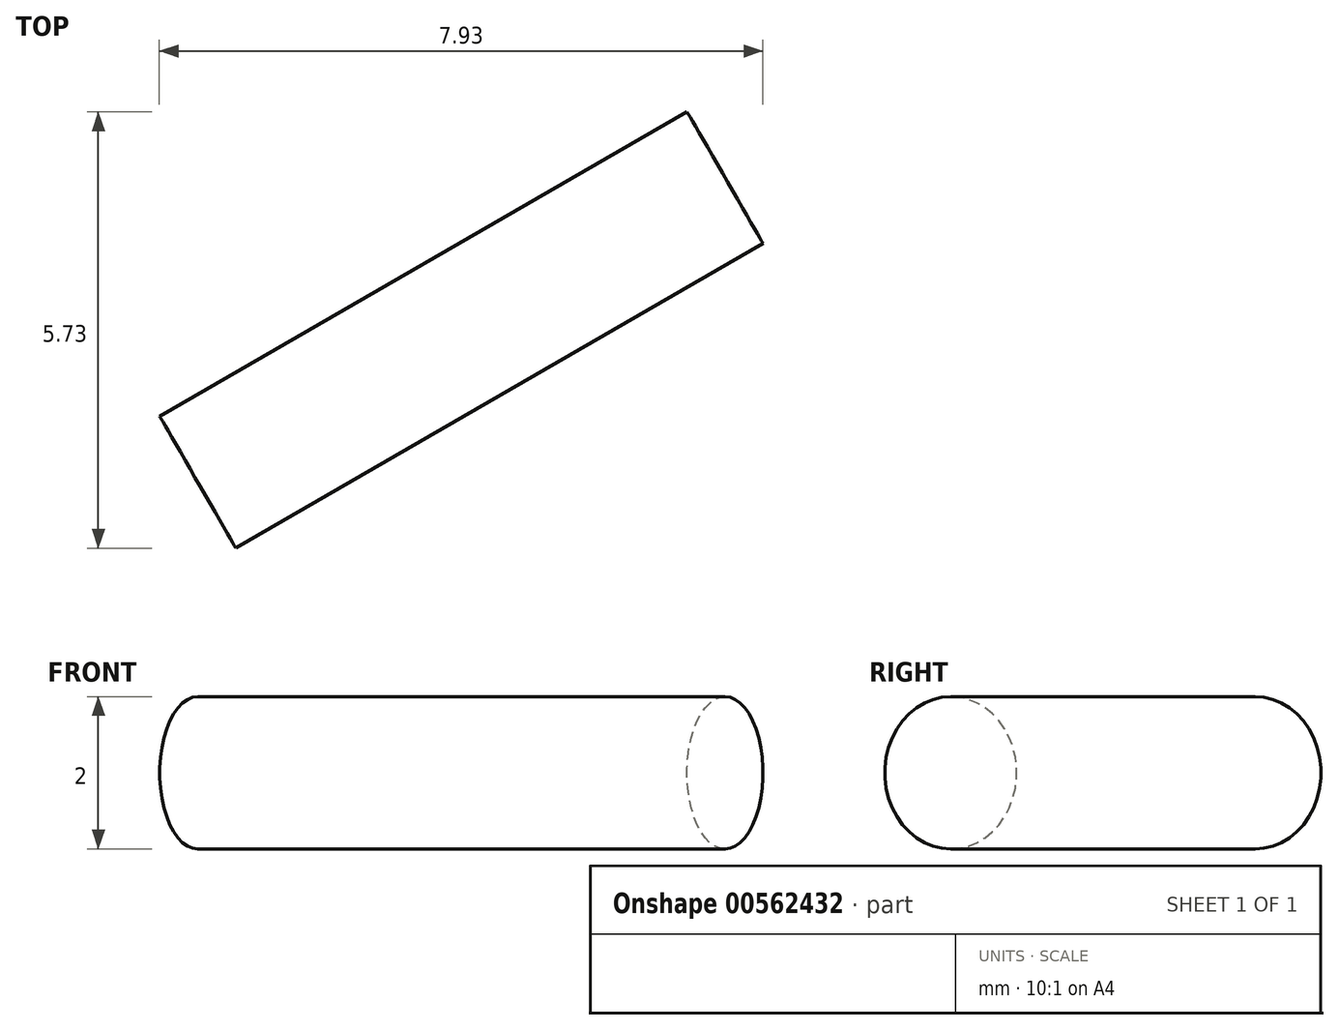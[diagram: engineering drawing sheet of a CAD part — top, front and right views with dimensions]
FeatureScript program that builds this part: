
annotation { "Feature Type Name" : "Feature", "Feature Type Description" : "" }
export const myFeature = defineFeature(function(context is Context, id is Id, definition is map)
    precondition{}
    {
        {
            var Q0;
            Q0=qCreatedBy(makeId("Right.planeOp"),FACE);
            var sketch = newSketch(context, id + "F0", { "sketchPlane" : qUnion([Q0])});
            skCircle(sketch, "E0", {"center": v(0, 0) * mm, "radius": 1 * mm});
            skSolve(sketch);
        }
        {
            var Q0;
            Q0 = qSketchRegion(id + "F0", true);
            extrude(context, id + "F1", {"entities" : qUnion([Q0]), "depth" : 8 * mm, "offsetDistance" : 25 * mm});
        }
        {
            var Q0;
            Q0=makeQuery(id+"F1.opExtrude","SWEPT_BODY",BODY,{"disambiguationData":[OSD([sQuery(id+"F0.wireOp",EDGE,"E0")])]});
            var Q1;
            Q1=makeQuery(id+"F1.opExtrude","CAP_EDGE",EDGE,{"disambiguationData":[OSD([sQuery(id+"F0.wireOp",EDGE,"E0")])],"isStart":true});
            transform(context, id + "F2", {"entities" : qUnion([Q0]), "transformType" : TransformType.ROTATION, "transformAxis" : qUnion([Q1]), "angle" : 45 * degree, "makeCopy" : true});
        }
        {
            var Q0;
            Q0=qCreatedBy(makeId("Right.planeOp"),FACE);
            var sketch = newSketch(context, id + "F3", { "sketchPlane" : qUnion([Q0])});
            skLineSegment(sketch, "E1.bottom", {"start": v(4.5, -1.48) * mm, "end": v(-8.5, -1.48) * mm});
            skLineSegment(sketch, "E1.top", {"start": v(4.5, 1.52) * mm, "end": v(-8.5, 1.52) * mm});
            skLineSegment(sketch, "E1.left", {"start": v(4.5, -1.48) * mm, "end": v(4.5, 1.52) * mm});
            skLineSegment(sketch, "E1.right", {"start": v(-8.5, -1.48) * mm, "end": v(-8.5, 1.52) * mm});
            skSolve(sketch);
        }
        {
            var Q0;
            Q0 = qSketchRegion(id + "F3", true);
            extrude(context, id + "F4", {"entities" : qUnion([Q0]), "endBound" : BoundingType.SYMMETRIC, "depth" : 2.5 * mm, "offsetDistance" : 25 * mm});
        }
        {
            var Q0;
            Q0=makeQuery(id+"F1.opExtrude","SWEPT_BODY",BODY,{"disambiguationData":[OSD([sQuery(id+"F0.wireOp",EDGE,"E0")])]});
            var Q1;
            Q1=makeQuery(id+"F4.opExtrude","CAP_EDGE",EDGE,{"disambiguationData":[OSD([sQuery(id+"F3.wireOp",EDGE,"E1.left")])],"isStart":true});
            transform(context, id + "F5", {"entities" : qUnion([Q0]), "transformType" : TransformType.ROTATION, "transformAxis" : qUnion([Q1]), "angle" : 30 * degree, "makeCopy" : false});
        }
        {
            var Q0;
            Q0=makeQuery(id+"F4.opExtrude","CAP_EDGE",EDGE,{"disambiguationData":[OSD([sQuery(id+"F3.wireOp",EDGE,"E1.bottom")])],"isStart":true});
            var Q1;
            Q1=makeQuery(id+"F4.opExtrude","CAP_EDGE",EDGE,{"disambiguationData":[OSD([sQuery(id+"F3.wireOp",EDGE,"E1.bottom")])],"isStart":false});
            var Q2;
            Q2=makeQuery(id+"F4.opExtrude","CAP_EDGE",EDGE,{"disambiguationData":[OSD([sQuery(id+"F3.wireOp",EDGE,"E1.top")])],"isStart":true});
            var Q3;
            Q3=makeQuery(id+"F4.opExtrude","CAP_EDGE",EDGE,{"disambiguationData":[OSD([sQuery(id+"F3.wireOp",EDGE,"E1.top")])],"isStart":false});
            chamfer(context, id + "F6", {"entities" : qUnion([Q0, Q1, Q2, Q3]), "width" : .5 * mm, "tangentPropagation" : true});
        }
        {
            var Q0;
            Q0=makeQuery(id+"F4.opExtrude","CAP_EDGE",EDGE,{"disambiguationData":[OSD([sQuery(id+"F3.wireOp",EDGE,"E1.right")])],"isStart":true});
            var Q1;
            Q1=makeQuery(id+"F4.opExtrude","CAP_EDGE",EDGE,{"disambiguationData":[OSD([sQuery(id+"F3.wireOp",EDGE,"E1.right")])],"isStart":false});
            var Q2;
            Q2=makeQuery(id+"F6.opChamfer","BLEND_EDGE",EDGE,{"blendedFrom":[makeQuery(id+"F4.opExtrude","CAP_EDGE",EDGE,{"disambiguationData":[OSD([sQuery(id+"F3.wireOp",EDGE,"E1.top")])],"isStart":true}),makeQuery(id+"F4.opExtrude","SWEPT_FACE",FACE,{"disambiguationData":[OSD([sQuery(id+"F3.wireOp",EDGE,"E1.right")])]})],"blendedInto":[makeQuery(id+"F4.opExtrude","SWEPT_FACE",FACE,{"disambiguationData":[OSD([sQuery(id+"F3.wireOp",EDGE,"E1.right")])]})]});
            var Q3;
            Q3=makeQuery(id+"F6.opChamfer","BLEND_EDGE",EDGE,{"blendedFrom":[makeQuery(id+"F4.opExtrude","CAP_EDGE",EDGE,{"disambiguationData":[OSD([sQuery(id+"F3.wireOp",EDGE,"E1.bottom")])],"isStart":true}),makeQuery(id+"F4.opExtrude","SWEPT_FACE",FACE,{"disambiguationData":[OSD([sQuery(id+"F3.wireOp",EDGE,"E1.right")])]})],"blendedInto":[makeQuery(id+"F4.opExtrude","SWEPT_FACE",FACE,{"disambiguationData":[OSD([sQuery(id+"F3.wireOp",EDGE,"E1.right")])]})]});
            var Q4;
            Q4=makeQuery(id+"F6.opChamfer","BLEND_EDGE",EDGE,{"blendedFrom":[makeQuery(id+"F4.opExtrude","CAP_EDGE",EDGE,{"disambiguationData":[OSD([sQuery(id+"F3.wireOp",EDGE,"E1.top")])],"isStart":false}),makeQuery(id+"F4.opExtrude","SWEPT_FACE",FACE,{"disambiguationData":[OSD([sQuery(id+"F3.wireOp",EDGE,"E1.right")])]})],"blendedInto":[makeQuery(id+"F4.opExtrude","SWEPT_FACE",FACE,{"disambiguationData":[OSD([sQuery(id+"F3.wireOp",EDGE,"E1.right")])]})]});
            var Q5;
            Q5=makeQuery(id+"F6.opChamfer","BLEND_EDGE",EDGE,{"blendedFrom":[makeQuery(id+"F4.opExtrude","CAP_EDGE",EDGE,{"disambiguationData":[OSD([sQuery(id+"F3.wireOp",EDGE,"E1.bottom")])],"isStart":false}),makeQuery(id+"F4.opExtrude","SWEPT_FACE",FACE,{"disambiguationData":[OSD([sQuery(id+"F3.wireOp",EDGE,"E1.right")])]})],"blendedInto":[makeQuery(id+"F4.opExtrude","SWEPT_FACE",FACE,{"disambiguationData":[OSD([sQuery(id+"F3.wireOp",EDGE,"E1.right")])]})]});
            chamfer(context, id + "F7", {"entities" : qUnion([Q0, Q1, Q2, Q3, Q4, Q5]), "chamferType" : ChamferType.TWO_OFFSETS, "width1" : .5 * mm, "oppositeDirection" : false, "width2" : .5 * mm, "tangentPropagation" : true});
        }
        {
            var Q0;
            Q0=makeQuery(id+"F6.opChamfer","BLEND_EDGE",EDGE,{"blendedFrom":[makeQuery(id+"F4.opExtrude","CAP_EDGE",EDGE,{"disambiguationData":[OSD([sQuery(id+"F3.wireOp",EDGE,"E1.top")])],"isStart":true}),makeQuery(id+"F4.opExtrude","SWEPT_FACE",FACE,{"disambiguationData":[OSD([sQuery(id+"F3.wireOp",EDGE,"E1.left")])]})],"blendedInto":[makeQuery(id+"F4.opExtrude","SWEPT_FACE",FACE,{"disambiguationData":[OSD([sQuery(id+"F3.wireOp",EDGE,"E1.left")])]})]});
            var Q1;
            Q1=makeQuery(id+"F6.opChamfer","BLEND_EDGE",EDGE,{"blendedFrom":[makeQuery(id+"F4.opExtrude","CAP_EDGE",EDGE,{"disambiguationData":[OSD([sQuery(id+"F3.wireOp",EDGE,"E1.top")])],"isStart":false}),makeQuery(id+"F4.opExtrude","SWEPT_FACE",FACE,{"disambiguationData":[OSD([sQuery(id+"F3.wireOp",EDGE,"E1.left")])]})],"blendedInto":[makeQuery(id+"F4.opExtrude","SWEPT_FACE",FACE,{"disambiguationData":[OSD([sQuery(id+"F3.wireOp",EDGE,"E1.left")])]})]});
            var Q2;
            Q2=makeQuery(id+"F6.opChamfer","BLEND_EDGE",EDGE,{"blendedFrom":[makeQuery(id+"F4.opExtrude","CAP_EDGE",EDGE,{"disambiguationData":[OSD([sQuery(id+"F3.wireOp",EDGE,"E1.bottom")])],"isStart":true}),makeQuery(id+"F4.opExtrude","SWEPT_FACE",FACE,{"disambiguationData":[OSD([sQuery(id+"F3.wireOp",EDGE,"E1.left")])]})],"blendedInto":[makeQuery(id+"F4.opExtrude","SWEPT_FACE",FACE,{"disambiguationData":[OSD([sQuery(id+"F3.wireOp",EDGE,"E1.left")])]})]});
            var Q3;
            Q3=makeQuery(id+"F6.opChamfer","BLEND_EDGE",EDGE,{"blendedFrom":[makeQuery(id+"F4.opExtrude","CAP_EDGE",EDGE,{"disambiguationData":[OSD([sQuery(id+"F3.wireOp",EDGE,"E1.bottom")])],"isStart":false}),makeQuery(id+"F4.opExtrude","SWEPT_FACE",FACE,{"disambiguationData":[OSD([sQuery(id+"F3.wireOp",EDGE,"E1.left")])]})],"blendedInto":[makeQuery(id+"F4.opExtrude","SWEPT_FACE",FACE,{"disambiguationData":[OSD([sQuery(id+"F3.wireOp",EDGE,"E1.left")])]})]});
            var Q4;
            {var subQ0=sQuery(id+"F3.wireOp",EDGE,"E1.right");Q4=makeQuery(id+"F7.opChamfer","BLEND_EDGE",EDGE,{"blendedFrom":[makeQuery(id+"F4.opExtrude","CAP_EDGE",EDGE,{"disambiguationData":[OSD([subQ0])],"isStart":true}),makeQuery(id+"F4.opExtrude","CAP_FACE",FACE,{"disambiguationData":[OSD([sQuery(id+"F3.wireOp",EDGE,"E1.bottom"),sQuery(id+"F3.wireOp",EDGE,"E1.top"),sQuery(id+"F3.wireOp",EDGE,"E1.left"),subQ0])],"isStart":true})],"blendedInto":[makeQuery(id+"F4.opExtrude","CAP_FACE",FACE,{"disambiguationData":[OSD([sQuery(id+"F3.wireOp",EDGE,"E1.bottom"),sQuery(id+"F3.wireOp",EDGE,"E1.top"),sQuery(id+"F3.wireOp",EDGE,"E1.left"),subQ0])],"isStart":true})]});}
            var Q5;
            {var subQ0=sQuery(id+"F3.wireOp",EDGE,"E1.right");Q5=makeQuery(id+"F7.opChamfer","BLEND_EDGE",EDGE,{"blendedFrom":[makeQuery(id+"F4.opExtrude","CAP_EDGE",EDGE,{"disambiguationData":[OSD([subQ0])],"isStart":false}),makeQuery(id+"F4.opExtrude","CAP_FACE",FACE,{"disambiguationData":[OSD([sQuery(id+"F3.wireOp",EDGE,"E1.bottom"),sQuery(id+"F3.wireOp",EDGE,"E1.top"),sQuery(id+"F3.wireOp",EDGE,"E1.left"),subQ0])],"isStart":false})],"blendedInto":[makeQuery(id+"F4.opExtrude","CAP_FACE",FACE,{"disambiguationData":[OSD([sQuery(id+"F3.wireOp",EDGE,"E1.bottom"),sQuery(id+"F3.wireOp",EDGE,"E1.top"),sQuery(id+"F3.wireOp",EDGE,"E1.left"),subQ0])],"isStart":false})]});}
            fillet(context, id + "F8", {"entities" : qUnion([Q0, Q1, Q2, Q3, Q4, Q5]), "radius" : 2.5 * mm, "tangentPropagation" : true, "allowEdgeOverflow" : false});
        }
        {
            var Q0;
            Q0=makeQuery(id+"F1.opExtrude","SWEPT_BODY",BODY,{"disambiguationData":[OSD([sQuery(id+"F0.wireOp",EDGE,"E0")])]});
            var Q1;
            Q1=qCreatedBy(makeId("Right.planeOp"),FACE);
            transform(context, id + "F9", {"entities" : qUnion([Q0]), "transformType" : TransformType.TRANSLATION_DISTANCE, "transformDirection" : qUnion([Q1]), "distance" : 1.75 * mm, "oppositeDirection" : true, "makeCopy" : false});
        }
        {
            var Q0;
            Q0=qCreatedBy(makeId("Front.planeOp"),FACE);
            var sketch = newSketch(context, id + "F10", { "sketchPlane" : qUnion([Q0])});
            skCircle(sketch, "E2", {"center": v(0, 0) * mm, "radius": 1 * mm});
            skSolve(sketch);
        }
        {
            var Q0;
            Q0 = qSketchRegion(id + "F10", true);
            extrude(context, id + "F11", {"entities" : qUnion([Q0]), "operationType" : NewBodyOperationType.ADD, "depth" : 10 * mm, "offsetDistance" : 25 * mm});
        }
        {
            var Q0;
            Q0=makeQuery(id+"F11.opExtrude","CAP_FACE",FACE,{"disambiguationData":[OSD([sQuery(id+"F10.wireOp",EDGE,"E2")])],"isStart":false});
            shell(context, id + "F12", {"entities" : qUnion([Q0]), "thickness" : .25 * mm});
        }
        {
            var Q0;
            Q0=makeQuery(id+"F2.opPattern","COPY",BODY,{"derivedFrom":makeQuery(id+"F1.opExtrude","SWEPT_BODY",BODY,{"disambiguationData":[OSD([sQuery(id+"F0.wireOp",EDGE,"E0")])]}),"instanceName":"1"});
            deleteBodies(context, id + "F13", {"entities" : qUnion([Q0])});
        }
    });
